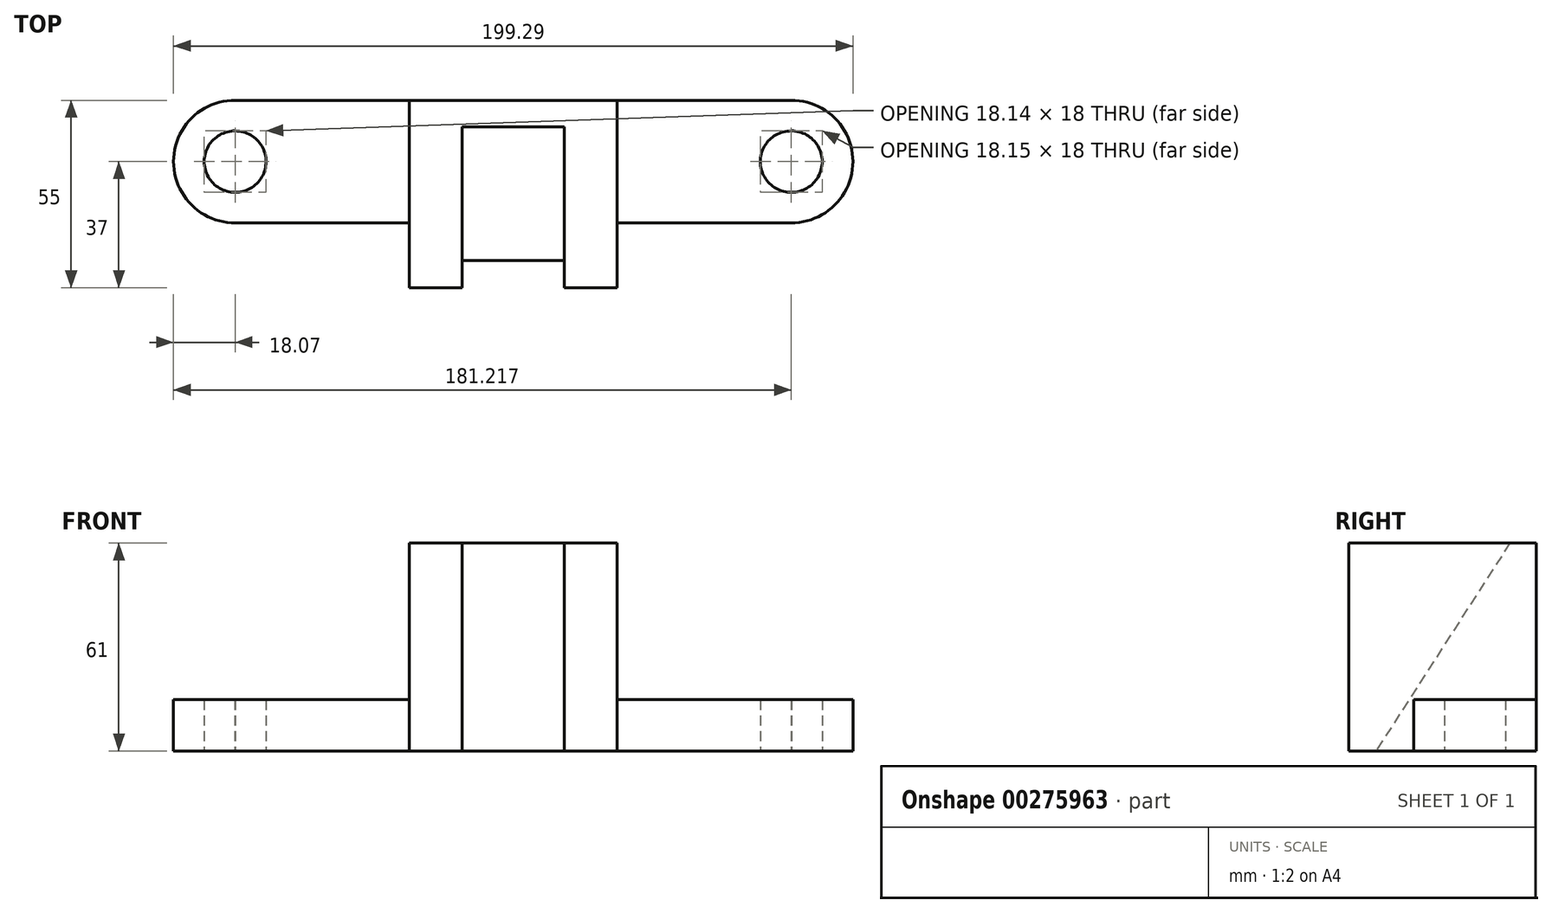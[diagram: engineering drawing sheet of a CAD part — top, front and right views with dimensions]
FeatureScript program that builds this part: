
annotation { "Feature Type Name" : "Feature", "Feature Type Description" : "" }
export const myFeature = defineFeature(function(context is Context, id is Id, definition is map)
    precondition{}
    {
        {
            var Q0;
            Q0=qCreatedBy(makeId("Front.planeOp"),FACE);
            var sketch = newSketch(context, id + "F0", { "sketchPlane" : qUnion([Q0])});
            skLineSegment(sketch, "E0.bottom", {"start": v(-30.5, 61) * mm, "end": v(30.5, 61) * mm});
            skLineSegment(sketch, "E0.top", {"start": v(-81.5, 0) * mm, "end": v(81.5, 0) * mm});
            skLineSegment(sketch, "E0.left", {"start": v(-81.5, 15) * mm, "end": v(-81.5, 0) * mm});
            skLineSegment(sketch, "E0.right", {"start": v(81.5, 15) * mm, "end": v(81.5, 0) * mm});
            skLineSegment(sketch, "E1.top", {"start": v(-81.5, 15) * mm, "end": v(-30.5, 15) * mm});
            skLineSegment(sketch, "E1.right", {"start": v(-30.5, 61) * mm, "end": v(-30.5, 15) * mm});
            skLineSegment(sketch, "E2.top", {"start": v(81.5, 15) * mm, "end": v(30.5, 15) * mm});
            skLineSegment(sketch, "E2.right", {"start": v(30.5, 61) * mm, "end": v(30.5, 15) * mm});
            skSolve(sketch);
        }
        {
            var Q0;
            Q0 = qSketchRegion(id + "F0", true);
            extrude(context, id + "F1", {"entities" : qUnion([Q0]), "depth" : 55 * mm});
        }
        {
            var Q0;
            Q0=qCreatedBy(makeId("Top.planeOp"),FACE);
            var sketch = newSketch(context, id + "F2", { "sketchPlane" : qUnion([Q0])});
            skCircle(sketch, "E3", {"center": v(-81.64, -18) * mm, "radius": 18 * mm});
            skCircle(sketch, "E4", {"center": v(81.65, -18) * mm, "radius": 18 * mm});
            skPoint(sketch, "E5.orphan", {"position": v(-15, -7.75) * mm});
            skPoint(sketch, "E6.orphan", {"position": v(15, -7.75) * mm});
            skPoint(sketch, "E7.end.orphan", {"position": v(15, -47) * mm});
            skPoint(sketch, "E7.start.orphan", {"position": v(-15, -47) * mm});
            skPoint(sketch, "E8.end.orphan", {"position": v(81.5, -36) * mm});
            skPoint(sketch, "E8.start.orphan", {"position": v(-81.5, -36) * mm});
            skCircle(sketch, "E9", {"center": v(-81.64, -18) * mm, "radius": 9 * mm});
            skCircle(sketch, "E10", {"center": v(81.65, -18) * mm, "radius": 9 * mm});
            skSolve(sketch);
        }
        {
            var Q0;
            Q0 = qSketchRegion(id + "F2", true);
            extrude(context, id + "F3", {"entities" : qUnion([Q0]), "operationType" : NewBodyOperationType.ADD, "depth" : 15 * mm});
        }
        {
            var Q0;
            Q0=qCreatedBy(makeId("Top.planeOp"),FACE);
            var sketch = newSketch(context, id + "F4", { "sketchPlane" : qUnion([Q0])});
            skCircle(sketch, "E11", {"center": v(-81.5, -18) * mm, "radius": 9 * mm});
            skCircle(sketch, "E12", {"center": v(81.5, -18) * mm, "radius": 9 * mm});
            skLineSegment(sketch, "E13.bottom", {"start": v(-81.5, -36) * mm, "end": v(-30.5, -36) * mm});
            skLineSegment(sketch, "E13.top", {"start": v(-81.5, -55) * mm, "end": v(-30.5, -55) * mm});
            skLineSegment(sketch, "E13.left", {"start": v(-81.5, -36) * mm, "end": v(-81.5, -55) * mm});
            skLineSegment(sketch, "E13.right", {"start": v(-30.5, -36) * mm, "end": v(-30.5, -55) * mm});
            skLineSegment(sketch, "E14", {"start": v(81.5, -55) * mm, "end": v(30.5, -55) * mm});
            skPoint(sketch, "E15.right.start.orphan", {"position": v(81.5, -47) * mm});
            skPoint(sketch, "E15.left.start.orphan", {"position": v(30.5, -47) * mm});
            skLineSegment(sketch, "E16", {"start": v(81.5, -36) * mm, "end": v(81.5, -55) * mm});
            skLineSegment(sketch, "E17", {"start": v(30.5, -36) * mm, "end": v(30.5, -55) * mm});
            skLineSegment(sketch, "E18", {"start": v(30.5, -36) * mm, "end": v(81.5, -36) * mm});
            skSolve(sketch);
        }
        {
            var Q0;
            Q0 = qSketchRegion(id + "F4", true);
            extrude(context, id + "F5", {"entities" : qUnion([Q0]), "operationType" : NewBodyOperationType.REMOVE, "depth" : 15 * mm});
        }
        {
            var Q0;
            Q0=makeQuery(id+"F5.boolean.opBoolean","MERGE",FACE,{"derivedFrom":[makeQuery(id+"F1.opExtrude","SWEPT_FACE",FACE,{"disambiguationData":[OSD([sQuery(id+"F0.wireOp",EDGE,"E1.right")])]}),makeQuery(id+"F5.opExtrude","SWEPT_FACE",FACE,{"disambiguationData":[OSD([sQuery(id+"F4.wireOp",EDGE,"E13.right")])]})]});
            var sketch = newSketch(context, id + "F6", { "sketchPlane" : qUnion([Q0])});
            skLineSegment(sketch, "E19", {"start": v(7.75, 61) * mm, "end": v(47, 0) * mm});
            skLineSegment(sketch, "E20", {"start": v(7.75, 61) * mm, "end": v(55, 61) * mm});
            skLineSegment(sketch, "E21", {"start": v(55, 61) * mm, "end": v(55, 0) * mm});
            skLineSegment(sketch, "E22", {"start": v(55, 0) * mm, "end": v(47, 0) * mm});
            skSolve(sketch);
        }
        {
            var Q0;
            Q0 = qSketchRegion(id + "F6", true);
            extrude(context, id + "F7", {"entities" : qUnion([Q0]), "operationType" : NewBodyOperationType.REMOVE, "oppositeDirection" : true, "depth" : 45.5 * mm, "hasSecondDirection" : true, "secondDirectionOppositeDirection" : true, "secondDirectionDepth" : 15.5 * mm});
        }
    });
